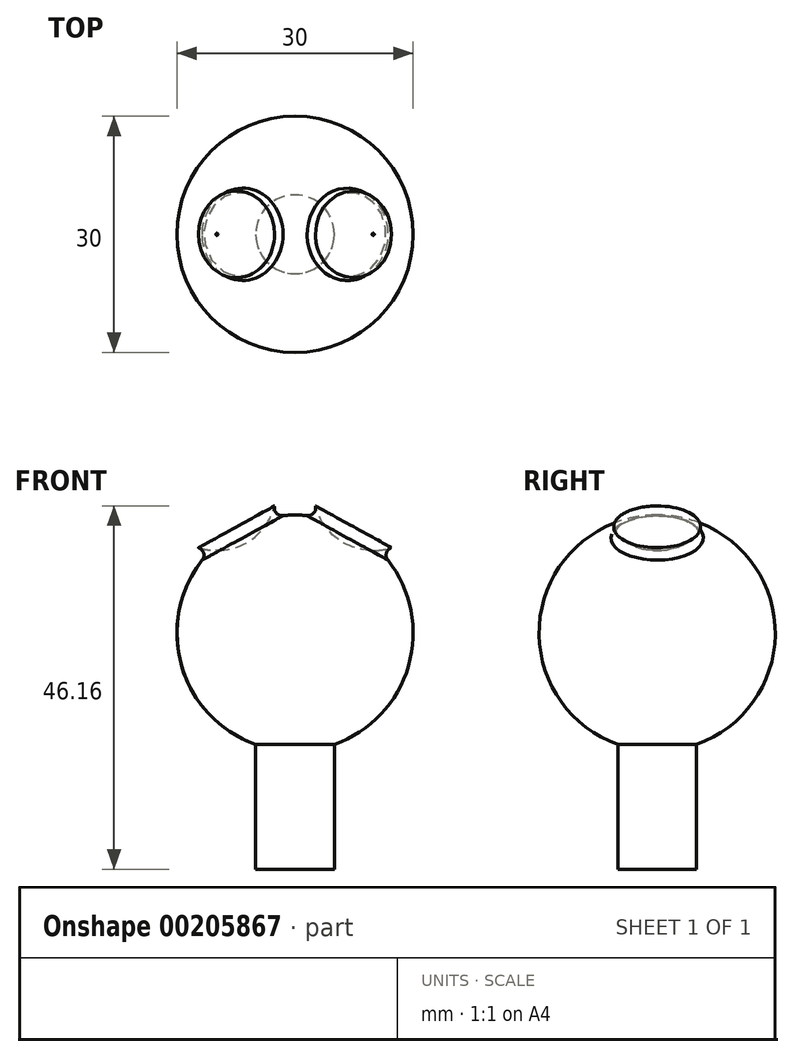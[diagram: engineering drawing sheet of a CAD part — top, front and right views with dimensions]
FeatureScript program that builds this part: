
annotation { "Feature Type Name" : "Feature", "Feature Type Description" : "" }
export const myFeature = defineFeature(function(context is Context, id is Id, definition is map)
    precondition{}
    {
        {
            var Q0;
            Q0=qCreatedBy(makeId("Front.planeOp"),FACE);
            var sketch = newSketch(context, id + "F0", { "sketchPlane" : qUnion([Q0])});
            skArc(sketch, "E0", {"start": v(-9.93, 25.5) * mm, "mid": v(-17.5, 18) * mm, "end": v(-9.93, 10.5) * mm});
            skLineSegment(sketch, "E1", {"start": v(0, 37.86) * mm, "end": v(0, 15) * mm, "construction": true});
            skLineSegment(sketch, "E2", {"start": v(-9.93, 30.6) * mm, "end": v(-9.93, 25.5) * mm, "construction": true});
            skLineSegment(sketch, "E3", {"start": v(0, 15) * mm, "end": v(0, -15) * mm});
            skLineSegment(sketch, "E4", {"start": v(-9.93, 25.5) * mm, "end": v(-9.93, 10.5) * mm});
            skLineSegment(sketch, "E5.trimOffspring", {"start": v(0, -15) * mm, "end": v(0, -28.48) * mm, "construction": true});
            skArc(sketch, "E6.trimOffspring", {"start": v(0, 15) * mm, "mid": v(-15, 0) * mm, "end": v(0, -15) * mm});
            skLineSegment(sketch, "E7.trimOffspring", {"start": v(-9.93, 11.24) * mm, "end": v(-9.93, 2.88) * mm, "construction": true});
            skSolve(sketch);
        }
        {
            var Q0;
            {var subQ1=sQuery(id+"F0.wireOp",EDGE,"E3");Q0=makeQuery(id+"F0.imprint","IMPRINT",FACE,{"disambiguationData":[TD([[makeQuery(id+"F0.imprint","IMPRINT",EDGE,{"derivedFrom":subQ1}),-1.0]])]});}
            var Q1;
            {var subQ0=sQuery(id+"F0.wireOp",EDGE,"E4");var subQ1=sQuery(id+"F0.wireOp",EDGE,"E0");var subQ2=makeQuery(id+"F0.imprint","INTERSECT",VERTEX,{"disambiguationData":[OD(1.0)],"derivedFrom":[subQ1,subQ0]});Q1=makeQuery(id+"F0.imprint","IMPRINT",FACE,{"disambiguationData":[TD([[makeQuery(id+"F0.imprint","IMPRINT",EDGE,{"disambiguationData":[TD([[subQ2,1.0]])],"derivedFrom":subQ1}),1.0]])]});}
            var Q2;
            Q2=sQuery(id+"F0.wireOp",EDGE,"E1");
            revolve(context, id + "F1", {"entities" : qUnion([Q0, Q1]), "axis" : qUnion([Q2]), "revolveType" : RevolveType.FULL});
        }
        {
            var Q0;
            {var subQ0=sQuery(id+"F0.wireOp",EDGE,"E4");var subQ1=sQuery(id+"F0.wireOp",EDGE,"E0");var subQ2=makeQuery(id+"F0.imprint","INTERSECT",VERTEX,{"disambiguationData":[OD(0.0)],"derivedFrom":[subQ1,subQ0]});Q0=makeQuery(id+"F0.imprint","IMPRINT",FACE,{"disambiguationData":[TD([[makeQuery(id+"F0.imprint","IMPRINT",EDGE,{"disambiguationData":[TD([[subQ2,-1.0]])],"derivedFrom":subQ1}),1.0]])]});}
            var Q1;
            Q1=sQuery(id+"F0.wireOp",EDGE,"E2");
            revolve(context, id + "F2", {"entities" : qUnion([Q0]), "axis" : qUnion([Q1]), "revolveType" : RevolveType.FULL});
        }
        {
            var Q0;
            Q0=makeQuery(id+"F2.opRevolve","SWEPT_BODY",BODY,{"disambiguationData":[OSD([sQuery(id+"F0.wireOp",EDGE,"E0"),sQuery(id+"F0.wireOp",EDGE,"E4"),sQuery(id+"F0.wireOp",EDGE,"E6.trimOffspring")])]});
            var Q1;
            Q1=qCreatedBy(makeId("Right.planeOp"),FACE);
            mirror(context, id + "F3", {"operationType" : NewBodyOperationType.ADD, "entities" : qUnion([Q0]), "mirrorPlane" : qUnion([Q1])});
        }
        {
            var Q0;
            Q0=qCreatedBy(makeId("Top.planeOp"),FACE);
            var sketch = newSketch(context, id + "F4", { "sketchPlane" : qUnion([Q0])});
            skCircle(sketch, "E8", {"center": v(0, 0) * mm, "radius": 5 * mm});
            skSolve(sketch);
        }
        {
            var Q0;
            Q0 = qSketchRegion(id + "F4", true);
            extrude(context, id + "F5", {"entities" : qUnion([Q0]), "operationType" : NewBodyOperationType.ADD, "oppositeDirection" : true, "depth" : 30 * mm});
        }
        {
            var Q0;
            Q0=makeQuery(id+"F3.boolean.opBoolean","INTERSECT",EDGE,{"derivedFrom":[makeQuery(id+"F1.opRevolve","SWEPT_FACE",FACE,{"disambiguationData":[OSD([sQuery(id+"F0.wireOp",EDGE,"E6.trimOffspring")])]}),makeQuery(id+"F2.opRevolve","SWEPT_FACE",FACE,{"disambiguationData":[OSD([sQuery(id+"F0.wireOp",EDGE,"E0")])]})]});
            fillet(context, id + "F6", {"entities" : qUnion([Q0]), "radius" : 1 * mm, "tangentPropagation" : true, "allowEdgeOverflow" : false});
        }
        {
            var Q0;
            Q0=makeQuery(id+"F3.boolean.opBoolean","INTERSECT",EDGE,{"derivedFrom":[makeQuery(id+"F1.opRevolve","SWEPT_FACE",FACE,{"disambiguationData":[OSD([sQuery(id+"F0.wireOp",EDGE,"E6.trimOffspring")])]}),makeQuery(id+"F3.opPattern","COPY",FACE,{"derivedFrom":makeQuery(id+"F2.opRevolve","SWEPT_FACE",FACE,{"disambiguationData":[OSD([sQuery(id+"F0.wireOp",EDGE,"E0")])]}),"instanceName":"1"})]});
            fillet(context, id + "F7", {"entities" : qUnion([Q0]), "radius" : 1 * mm, "tangentPropagation" : true, "allowEdgeOverflow" : false});
        }
    });
